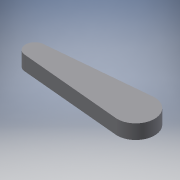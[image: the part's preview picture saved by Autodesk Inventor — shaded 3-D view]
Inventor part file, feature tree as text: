
AUTODESK INVENTOR PART (.ipt)
format: ipt  version: 2018.3 (Build 223284000, 284)  size: 94,720 bytes
history: native  units: mm
features: other x1, extrude x1, sketch x1
ambient origin geometry x8: Origin, YZ Plane, XZ Plane, XY Plane, X Axis, Y Axis, Z Axis, Center Point
bodies: Body1 (feature_tree)
feature tree (3):
  other  "Твердое тело1"
  extrude  "Выдавливание1"  Depth=26.0mm
  sketch  "Эскиз1"
